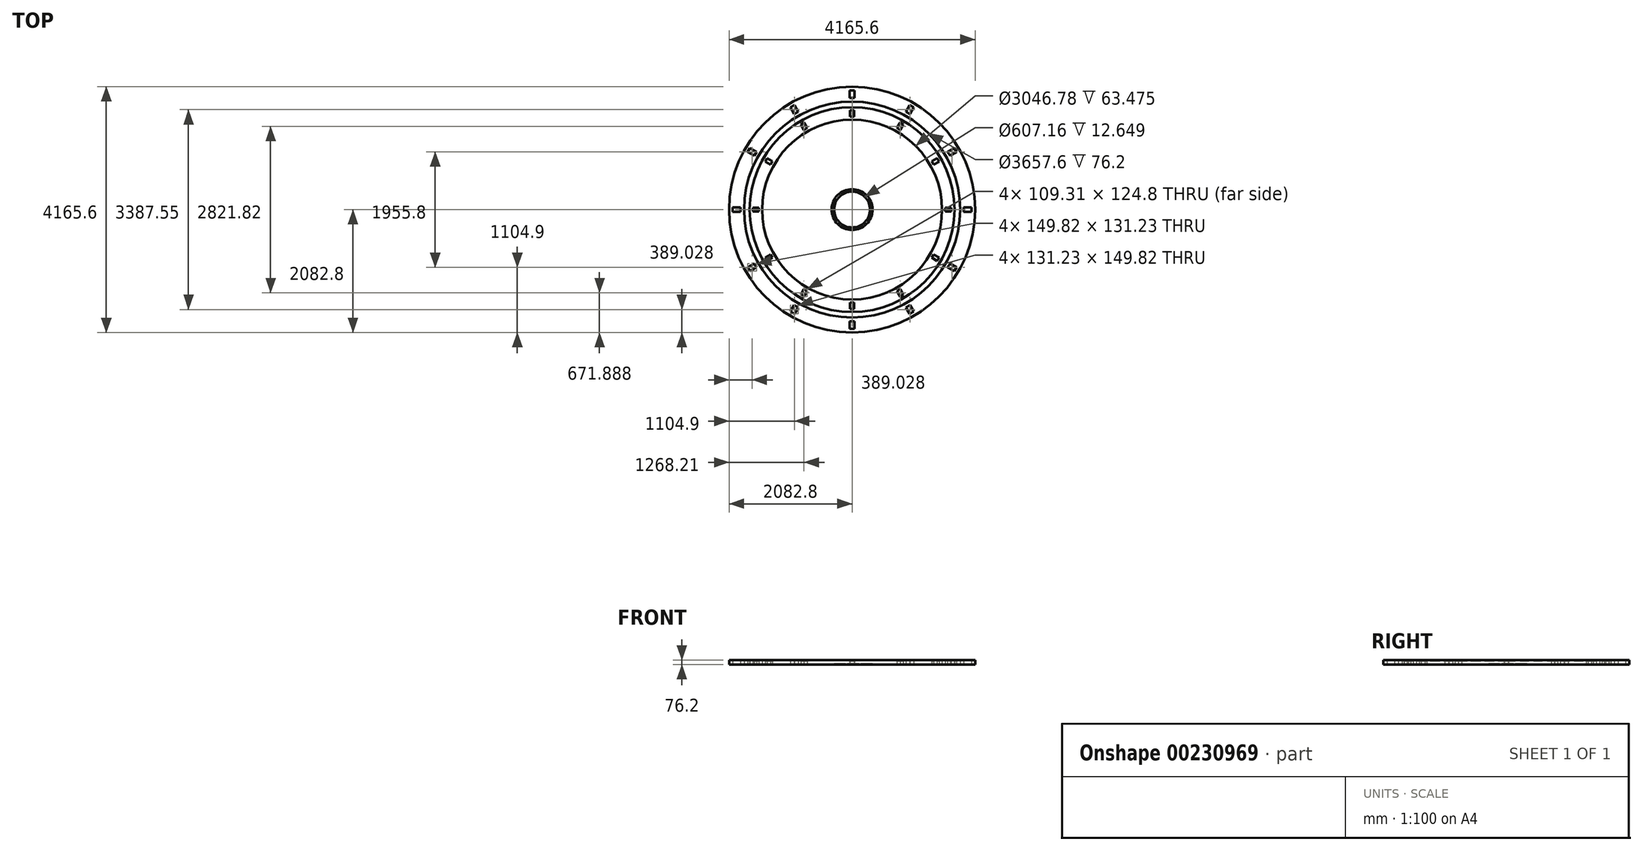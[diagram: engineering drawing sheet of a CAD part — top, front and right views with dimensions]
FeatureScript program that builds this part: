
annotation { "Feature Type Name" : "Feature", "Feature Type Description" : "" }
export const myFeature = defineFeature(function(context is Context, id is Id, definition is map)
    precondition{}
    {
        {
            var Q0;
            Q0=qCreatedBy(makeId("Top.planeOp"),FACE);
            var sketch = newSketch(context, id + "F0", { "sketchPlane" : qUnion([Q0])});
            skCircle(sketch, "E0", {"center": v(0, 0) * mm, "radius": 2082.8 * mm});
            skCircle(sketch, "E1", {"center": v(0, 0) * mm, "radius": 1828.8 * mm});
            skCircle(sketch, "E2", {"center": v(0, 0) * mm, "radius": 1955.8 * mm, "construction": true});
            skLineSegment(sketch, "E3.bottom", {"start": v(-2019.94, 38.74) * mm, "end": v(-1891.67, 38.74) * mm});
            skLineSegment(sketch, "E3.top", {"start": v(-2019.94, -38.73) * mm, "end": v(-1891.67, -38.73) * mm});
            skLineSegment(sketch, "E3.left", {"start": v(-2019.94, 38.74) * mm, "end": v(-2019.94, -38.73) * mm});
            skLineSegment(sketch, "E3.right", {"start": v(-1891.67, 38.74) * mm, "end": v(-1891.67, -38.73) * mm});
            skPoint(sketch, "E3.middle", {"position": v(-1955.8, 0) * mm});
            skLineSegment(sketch, "E4.1.0", {"start": v(-1768.68, -976.42) * mm, "end": v(-1657.6, -912.29) * mm});
            skLineSegment(sketch, "E4.1.1", {"start": v(-1657.6, -912.29) * mm, "end": v(-1618.86, -979.38) * mm});
            skLineSegment(sketch, "E4.1.2", {"start": v(-1729.95, -1043.51) * mm, "end": v(-1618.86, -979.38) * mm});
            skLineSegment(sketch, "E4.1.3", {"start": v(-1768.68, -976.42) * mm, "end": v(-1729.95, -1043.51) * mm});
            skLineSegment(sketch, "E4.2.0", {"start": v(-1043.51, -1729.95) * mm, "end": v(-979.38, -1618.86) * mm});
            skLineSegment(sketch, "E4.2.1", {"start": v(-979.38, -1618.86) * mm, "end": v(-912.29, -1657.6) * mm});
            skLineSegment(sketch, "E4.2.2", {"start": v(-976.42, -1768.68) * mm, "end": v(-912.29, -1657.6) * mm});
            skLineSegment(sketch, "E4.2.3", {"start": v(-1043.51, -1729.95) * mm, "end": v(-976.42, -1768.68) * mm});
            skLineSegment(sketch, "E4.3.0", {"start": v(-38.74, -2019.94) * mm, "end": v(-38.74, -1891.67) * mm});
            skLineSegment(sketch, "E4.3.1", {"start": v(-38.74, -1891.67) * mm, "end": v(38.73, -1891.67) * mm});
            skLineSegment(sketch, "E4.3.2", {"start": v(38.73, -2019.94) * mm, "end": v(38.73, -1891.67) * mm});
            skLineSegment(sketch, "E4.3.3", {"start": v(-38.74, -2019.94) * mm, "end": v(38.73, -2019.94) * mm});
            skLineSegment(sketch, "E4.4.0", {"start": v(976.42, -1768.68) * mm, "end": v(912.29, -1657.6) * mm});
            skLineSegment(sketch, "E4.4.1", {"start": v(912.29, -1657.6) * mm, "end": v(979.38, -1618.86) * mm});
            skLineSegment(sketch, "E4.4.2", {"start": v(1043.51, -1729.95) * mm, "end": v(979.38, -1618.86) * mm});
            skLineSegment(sketch, "E4.4.3", {"start": v(976.42, -1768.68) * mm, "end": v(1043.51, -1729.95) * mm});
            skLineSegment(sketch, "E4.5.0", {"start": v(1729.95, -1043.51) * mm, "end": v(1618.86, -979.38) * mm});
            skLineSegment(sketch, "E4.5.1", {"start": v(1618.86, -979.38) * mm, "end": v(1657.6, -912.29) * mm});
            skLineSegment(sketch, "E4.5.2", {"start": v(1768.68, -976.42) * mm, "end": v(1657.6, -912.29) * mm});
            skLineSegment(sketch, "E4.5.3", {"start": v(1729.95, -1043.51) * mm, "end": v(1768.68, -976.42) * mm});
            skLineSegment(sketch, "E4.6.0", {"start": v(2019.94, -38.74) * mm, "end": v(1891.67, -38.74) * mm});
            skLineSegment(sketch, "E4.6.1", {"start": v(1891.67, -38.74) * mm, "end": v(1891.67, 38.73) * mm});
            skLineSegment(sketch, "E4.6.2", {"start": v(2019.94, 38.73) * mm, "end": v(1891.67, 38.73) * mm});
            skLineSegment(sketch, "E4.6.3", {"start": v(2019.94, -38.74) * mm, "end": v(2019.94, 38.73) * mm});
            skLineSegment(sketch, "E4.7.0", {"start": v(1768.68, 976.42) * mm, "end": v(1657.6, 912.29) * mm});
            skLineSegment(sketch, "E4.7.1", {"start": v(1657.6, 912.29) * mm, "end": v(1618.86, 979.38) * mm});
            skLineSegment(sketch, "E4.7.2", {"start": v(1729.95, 1043.51) * mm, "end": v(1618.86, 979.38) * mm});
            skLineSegment(sketch, "E4.7.3", {"start": v(1768.68, 976.42) * mm, "end": v(1729.95, 1043.51) * mm});
            skLineSegment(sketch, "E4.8.0", {"start": v(1043.51, 1729.95) * mm, "end": v(979.38, 1618.86) * mm});
            skLineSegment(sketch, "E4.8.1", {"start": v(979.38, 1618.86) * mm, "end": v(912.29, 1657.6) * mm});
            skLineSegment(sketch, "E4.8.2", {"start": v(976.42, 1768.68) * mm, "end": v(912.29, 1657.6) * mm});
            skLineSegment(sketch, "E4.8.3", {"start": v(1043.51, 1729.95) * mm, "end": v(976.42, 1768.68) * mm});
            skLineSegment(sketch, "E4.9.0", {"start": v(38.74, 2019.94) * mm, "end": v(38.74, 1891.67) * mm});
            skLineSegment(sketch, "E4.9.1", {"start": v(38.74, 1891.67) * mm, "end": v(-38.73, 1891.67) * mm});
            skLineSegment(sketch, "E4.9.2", {"start": v(-38.73, 2019.94) * mm, "end": v(-38.73, 1891.67) * mm});
            skLineSegment(sketch, "E4.9.3", {"start": v(38.74, 2019.94) * mm, "end": v(-38.73, 2019.94) * mm});
            skLineSegment(sketch, "E4.10.0", {"start": v(-976.42, 1768.68) * mm, "end": v(-912.29, 1657.6) * mm});
            skLineSegment(sketch, "E4.10.1", {"start": v(-912.29, 1657.6) * mm, "end": v(-979.38, 1618.86) * mm});
            skLineSegment(sketch, "E4.10.2", {"start": v(-1043.51, 1729.95) * mm, "end": v(-979.38, 1618.86) * mm});
            skLineSegment(sketch, "E4.10.3", {"start": v(-976.42, 1768.68) * mm, "end": v(-1043.51, 1729.95) * mm});
            skLineSegment(sketch, "E4.11.0", {"start": v(-1729.95, 1043.51) * mm, "end": v(-1618.86, 979.38) * mm});
            skLineSegment(sketch, "E4.11.1", {"start": v(-1618.86, 979.38) * mm, "end": v(-1657.6, 912.29) * mm});
            skLineSegment(sketch, "E4.11.2", {"start": v(-1768.68, 976.42) * mm, "end": v(-1657.6, 912.29) * mm});
            skLineSegment(sketch, "E4.11.3", {"start": v(-1729.95, 1043.51) * mm, "end": v(-1768.68, 976.42) * mm});
            skSolve(sketch);
        }
        {
            var Q0;
            Q0=makeQuery(id+"F0.imprint","IMPRINT",FACE,{"disambiguationData":[TD([[makeQuery(id+"F0.imprint","IMPRINT",EDGE,{"derivedFrom":sQuery(id+"F0.wireOp",EDGE,"E0")}),1.0]])]});
            extrude(context, id + "F1", {"entities" : qUnion([Q0]), "depth" : 76.2 * mm});
        }
        {
            var Q0;
            Q0=makeQuery(id+"F1.opExtrude","SWEPT_BODY",BODY,{"disambiguationData":[OSD([sQuery(id+"F0.wireOp",EDGE,"E0"),sQuery(id+"F0.wireOp",EDGE,"E1"),sQuery(id+"F0.wireOp",EDGE,"E3.bottom"),sQuery(id+"F0.wireOp",EDGE,"E3.top"),sQuery(id+"F0.wireOp",EDGE,"E3.left"),sQuery(id+"F0.wireOp",EDGE,"E3.right"),sQuery(id+"F0.wireOp",EDGE,"E4.1.0"),sQuery(id+"F0.wireOp",EDGE,"E4.1.1"),sQuery(id+"F0.wireOp",EDGE,"E4.1.2"),sQuery(id+"F0.wireOp",EDGE,"E4.1.3"),sQuery(id+"F0.wireOp",EDGE,"E4.2.0"),sQuery(id+"F0.wireOp",EDGE,"E4.2.1"),sQuery(id+"F0.wireOp",EDGE,"E4.2.2"),sQuery(id+"F0.wireOp",EDGE,"E4.2.3"),sQuery(id+"F0.wireOp",EDGE,"E4.3.0"),sQuery(id+"F0.wireOp",EDGE,"E4.3.1"),sQuery(id+"F0.wireOp",EDGE,"E4.3.2"),sQuery(id+"F0.wireOp",EDGE,"E4.3.3"),sQuery(id+"F0.wireOp",EDGE,"E4.4.0"),sQuery(id+"F0.wireOp",EDGE,"E4.4.1"),sQuery(id+"F0.wireOp",EDGE,"E4.4.2"),sQuery(id+"F0.wireOp",EDGE,"E4.4.3"),sQuery(id+"F0.wireOp",EDGE,"E4.5.0"),sQuery(id+"F0.wireOp",EDGE,"E4.5.1"),sQuery(id+"F0.wireOp",EDGE,"E4.5.2"),sQuery(id+"F0.wireOp",EDGE,"E4.5.3"),sQuery(id+"F0.wireOp",EDGE,"E4.6.0"),sQuery(id+"F0.wireOp",EDGE,"E4.6.1"),sQuery(id+"F0.wireOp",EDGE,"E4.6.2"),sQuery(id+"F0.wireOp",EDGE,"E4.6.3"),sQuery(id+"F0.wireOp",EDGE,"E4.7.0"),sQuery(id+"F0.wireOp",EDGE,"E4.7.1"),sQuery(id+"F0.wireOp",EDGE,"E4.7.2"),sQuery(id+"F0.wireOp",EDGE,"E4.7.3"),sQuery(id+"F0.wireOp",EDGE,"E4.8.0"),sQuery(id+"F0.wireOp",EDGE,"E4.8.1"),sQuery(id+"F0.wireOp",EDGE,"E4.8.2"),sQuery(id+"F0.wireOp",EDGE,"E4.8.3"),sQuery(id+"F0.wireOp",EDGE,"E4.9.0"),sQuery(id+"F0.wireOp",EDGE,"E4.9.1"),sQuery(id+"F0.wireOp",EDGE,"E4.9.2"),sQuery(id+"F0.wireOp",EDGE,"E4.9.3"),sQuery(id+"F0.wireOp",EDGE,"E4.10.0"),sQuery(id+"F0.wireOp",EDGE,"E4.10.1"),sQuery(id+"F0.wireOp",EDGE,"E4.10.2"),sQuery(id+"F0.wireOp",EDGE,"E4.10.3"),sQuery(id+"F0.wireOp",EDGE,"E4.11.0"),sQuery(id+"F0.wireOp",EDGE,"E4.11.1"),sQuery(id+"F0.wireOp",EDGE,"E4.11.2"),sQuery(id+"F0.wireOp",EDGE,"E4.11.3")])]});
            var Q1;
            Q1=qCreatedBy(makeId("Origin.pointOp"),VERTEX);
            transform(context, id + "F2", {"entities" : qUnion([Q0]), "transformType" : TransformType.SCALE_UNIFORMLY, "scale" : .833, "scalePoint" : qUnion([Q1]), "makeCopy" : true});
        }
        {
            var Q0;
            Q0=makeQuery(id+"F1.opExtrude","SWEPT_BODY",BODY,{"disambiguationData":[OSD([sQuery(id+"F0.wireOp",EDGE,"E0"),sQuery(id+"F0.wireOp",EDGE,"E1"),sQuery(id+"F0.wireOp",EDGE,"E3.bottom"),sQuery(id+"F0.wireOp",EDGE,"E3.top"),sQuery(id+"F0.wireOp",EDGE,"E3.left"),sQuery(id+"F0.wireOp",EDGE,"E3.right"),sQuery(id+"F0.wireOp",EDGE,"E4.1.0"),sQuery(id+"F0.wireOp",EDGE,"E4.1.1"),sQuery(id+"F0.wireOp",EDGE,"E4.1.2"),sQuery(id+"F0.wireOp",EDGE,"E4.1.3"),sQuery(id+"F0.wireOp",EDGE,"E4.2.0"),sQuery(id+"F0.wireOp",EDGE,"E4.2.1"),sQuery(id+"F0.wireOp",EDGE,"E4.2.2"),sQuery(id+"F0.wireOp",EDGE,"E4.2.3"),sQuery(id+"F0.wireOp",EDGE,"E4.3.0"),sQuery(id+"F0.wireOp",EDGE,"E4.3.1"),sQuery(id+"F0.wireOp",EDGE,"E4.3.2"),sQuery(id+"F0.wireOp",EDGE,"E4.3.3"),sQuery(id+"F0.wireOp",EDGE,"E4.4.0"),sQuery(id+"F0.wireOp",EDGE,"E4.4.1"),sQuery(id+"F0.wireOp",EDGE,"E4.4.2"),sQuery(id+"F0.wireOp",EDGE,"E4.4.3"),sQuery(id+"F0.wireOp",EDGE,"E4.5.0"),sQuery(id+"F0.wireOp",EDGE,"E4.5.1"),sQuery(id+"F0.wireOp",EDGE,"E4.5.2"),sQuery(id+"F0.wireOp",EDGE,"E4.5.3"),sQuery(id+"F0.wireOp",EDGE,"E4.6.0"),sQuery(id+"F0.wireOp",EDGE,"E4.6.1"),sQuery(id+"F0.wireOp",EDGE,"E4.6.2"),sQuery(id+"F0.wireOp",EDGE,"E4.6.3"),sQuery(id+"F0.wireOp",EDGE,"E4.7.0"),sQuery(id+"F0.wireOp",EDGE,"E4.7.1"),sQuery(id+"F0.wireOp",EDGE,"E4.7.2"),sQuery(id+"F0.wireOp",EDGE,"E4.7.3"),sQuery(id+"F0.wireOp",EDGE,"E4.8.0"),sQuery(id+"F0.wireOp",EDGE,"E4.8.1"),sQuery(id+"F0.wireOp",EDGE,"E4.8.2"),sQuery(id+"F0.wireOp",EDGE,"E4.8.3"),sQuery(id+"F0.wireOp",EDGE,"E4.9.0"),sQuery(id+"F0.wireOp",EDGE,"E4.9.1"),sQuery(id+"F0.wireOp",EDGE,"E4.9.2"),sQuery(id+"F0.wireOp",EDGE,"E4.9.3"),sQuery(id+"F0.wireOp",EDGE,"E4.10.0"),sQuery(id+"F0.wireOp",EDGE,"E4.10.1"),sQuery(id+"F0.wireOp",EDGE,"E4.10.2"),sQuery(id+"F0.wireOp",EDGE,"E4.10.3"),sQuery(id+"F0.wireOp",EDGE,"E4.11.0"),sQuery(id+"F0.wireOp",EDGE,"E4.11.1"),sQuery(id+"F0.wireOp",EDGE,"E4.11.2"),sQuery(id+"F0.wireOp",EDGE,"E4.11.3")])]});
            var Q1;
            Q1=qCreatedBy(makeId("Origin.pointOp"),VERTEX);
            transform(context, id + "F3", {"entities" : qUnion([Q0]), "transformType" : TransformType.SCALE_UNIFORMLY, "scale" : .166, "scalePoint" : qUnion([Q1]), "makeCopy" : true});
        }
    });
